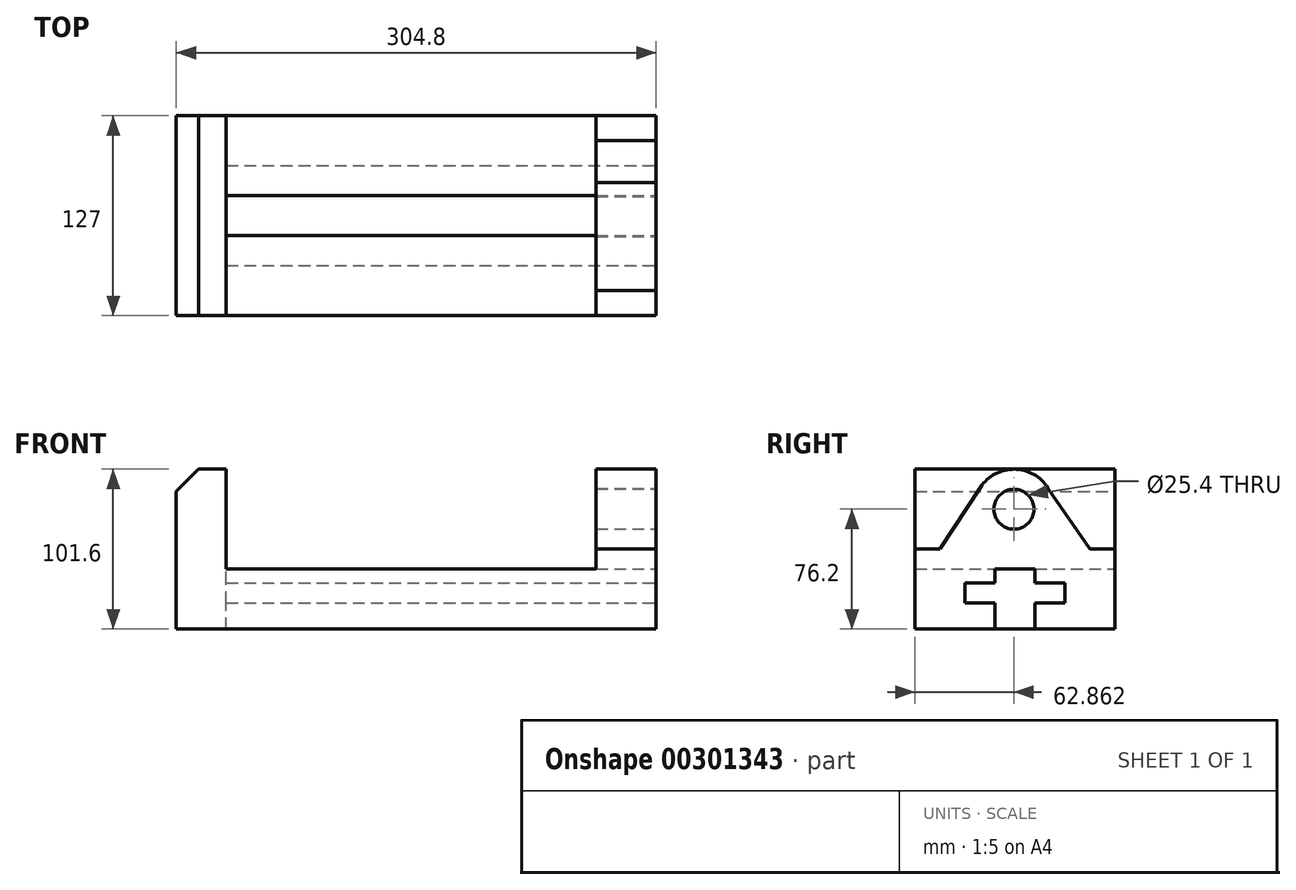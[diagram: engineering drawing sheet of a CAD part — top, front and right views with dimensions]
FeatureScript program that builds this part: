
annotation { "Feature Type Name" : "Feature", "Feature Type Description" : "" }
export const myFeature = defineFeature(function(context is Context, id is Id, definition is map)
    precondition{}
    {
        {
            var Q0;
            Q0=qCreatedBy(makeId("Front.planeOp"),FACE);
            var sketch = newSketch(context, id + "F0", { "sketchPlane" : qUnion([Q0])});
            skLineSegment(sketch, "E0", {"start": v(0, 0) * mm, "end": v(0, 101.6) * mm});
            skLineSegment(sketch, "E1", {"start": v(0, 101.6) * mm, "end": v(31.75, 101.6) * mm});
            skLineSegment(sketch, "E2", {"start": v(31.75, 101.6) * mm, "end": v(31.75, 38.1) * mm});
            skLineSegment(sketch, "E3", {"start": v(31.75, 38.1) * mm, "end": v(266.7, 38.1) * mm});
            skLineSegment(sketch, "E4", {"start": v(266.7, 38.1) * mm, "end": v(266.7, 101.6) * mm});
            skLineSegment(sketch, "E5", {"start": v(266.7, 101.6) * mm, "end": v(304.8, 101.6) * mm});
            skLineSegment(sketch, "E6", {"start": v(304.8, 101.6) * mm, "end": v(304.8, 0) * mm});
            skLineSegment(sketch, "E7", {"start": v(0, 0) * mm, "end": v(304.8, 0) * mm});
            skSolve(sketch);
        }
        {
            var Q0;
            Q0 = qSketchRegion(id + "F0", true);
            extrude(context, id + "F1", {"entities" : qUnion([Q0]), "depth" : 127 * mm});
        }
        {
            var Q0;
            Q0=makeQuery(id+"F1.opExtrude","SWEPT_EDGE",EDGE,{"disambiguationData":[OSD([sQuery(id+"F0.wireOp",EDGE,"E0"),sQuery(id+"F0.wireOp",EDGE,"E1")])]});
            chamfer(context, id + "F2", {"entities" : qUnion([Q0]), "width" : 14.29 * mm, "tangentPropagation" : true});
        }
        {
            var Q0;
            Q0=makeQuery(id+"F1.opExtrude","SWEPT_FACE",FACE,{"disambiguationData":[OSD([sQuery(id+"F0.wireOp",EDGE,"E6")])]});
            var sketch = newSketch(context, id + "F3", { "sketchPlane" : qUnion([Q0])});
            skLineSegment(sketch, "E8", {"start": v(0, 50.8) * mm, "end": v(-15.87, 50.8) * mm});
            skLineSegment(sketch, "E9", {"start": v(-127, 50.8) * mm, "end": v(-111.12, 50.8) * mm});
            skLineSegment(sketch, "E10", {"start": v(-111.12, 50.8) * mm, "end": v(-85.39, 90.11) * mm});
            skLineSegment(sketch, "E11", {"start": v(-15.87, 50.8) * mm, "end": v(-42.5, 89.51) * mm});
            skArc(sketch, "E12", {"start": v(-85.39, 90.11) * mm, "mid": v(-63.78, 101.6) * mm, "end": v(-42.5, 89.51) * mm});
            skLineSegment(sketch, "E13", {"start": v(-127, 50.8) * mm, "end": v(-127, 101.6) * mm});
            skLineSegment(sketch, "E14", {"start": v(-127, 101.6) * mm, "end": v(0, 101.6) * mm});
            skLineSegment(sketch, "E15", {"start": v(0, 101.6) * mm, "end": v(0, 50.8) * mm});
            skCircle(sketch, "E16", {"center": v(-64.14, 76.2) * mm, "radius": 12.7 * mm});
            skLineSegment(sketch, "E17", {"start": v(-76.2, 0) * mm, "end": v(-76.2, 16.51) * mm});
            skLineSegment(sketch, "E18", {"start": v(-76.2, 16.51) * mm, "end": v(-95.25, 16.51) * mm});
            skLineSegment(sketch, "E19", {"start": v(-95.25, 16.51) * mm, "end": v(-95.25, 29.21) * mm});
            skLineSegment(sketch, "E20", {"start": v(-95.25, 29.21) * mm, "end": v(-76.2, 29.21) * mm});
            skLineSegment(sketch, "E21", {"start": v(-76.2, 29.2) * mm, "end": v(-76.2, 38.1) * mm});
            skLineSegment(sketch, "E22", {"start": v(-76.2, 38.1) * mm, "end": v(-50.8, 38.1) * mm});
            skLineSegment(sketch, "E23", {"start": v(-50.8, 38.1) * mm, "end": v(-50.8, 29.2) * mm});
            skLineSegment(sketch, "E24", {"start": v(-50.8, 29.21) * mm, "end": v(-31.75, 29.21) * mm});
            skLineSegment(sketch, "E25", {"start": v(-31.75, 29.21) * mm, "end": v(-31.75, 16.51) * mm});
            skLineSegment(sketch, "E26", {"start": v(-31.75, 16.51) * mm, "end": v(-50.8, 16.51) * mm});
            skLineSegment(sketch, "E27", {"start": v(-50.8, 16.51) * mm, "end": v(-50.8, 0) * mm});
            skLineSegment(sketch, "E28", {"start": v(-50.8, 0) * mm, "end": v(-76.2, 0) * mm});
            skLineSegment(sketch, "E29", {"start": v(-63.5, 0) * mm, "end": v(-63.5, 55.08) * mm, "construction": true});
            skSolve(sketch);
        }
        {
            var Q0;
            Q0 = qSketchRegion(id + "F3", true);
            extrude(context, id + "F4", {"entities" : qUnion([Q0]), "operationType" : NewBodyOperationType.REMOVE, "oppositeDirection" : true, "depth" : 273.05 * mm});
        }
    });
